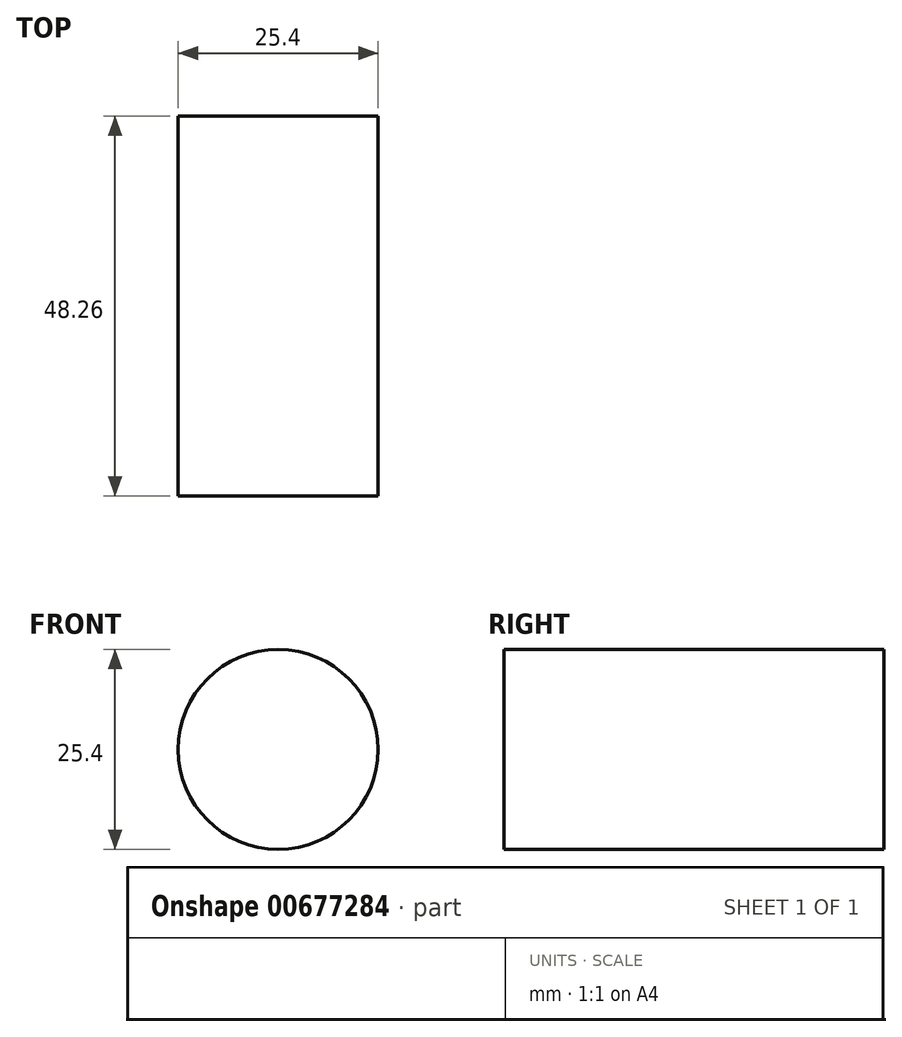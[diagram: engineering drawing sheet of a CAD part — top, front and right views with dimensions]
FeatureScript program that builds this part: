
annotation { "Feature Type Name" : "Feature", "Feature Type Description" : "" }
export const myFeature = defineFeature(function(context is Context, id is Id, definition is map)
    precondition{}
    {
        {
            var Q0;
            Q0=qCreatedBy(makeId("Front.planeOp"),FACE);
            var sketch = newSketch(context, id + "F0", { "sketchPlane" : qUnion([Q0])});
            skCircle(sketch, "E0", {"center": v(0, 0) * mm, "radius": 12.7 * mm});
            skSolve(sketch);
        }
        {
            var Q0;
            Q0=sQuery(id+"F0.wireOp",EDGE,"E0");
            extrude(context, id + "F1", {"bodyType" : ToolBodyType.SURFACE, "surfaceEntities" : qUnion([Q0]), "endBound" : BoundingType.SYMMETRIC, "depth" : 48.26 * mm, "offsetDistance" : 25.4 * mm});
        }
    });
